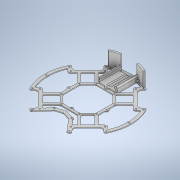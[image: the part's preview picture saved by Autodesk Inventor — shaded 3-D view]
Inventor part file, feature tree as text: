
AUTODESK INVENTOR PART (.ipt)
format: ipt  version: 2020 (Build 240168000, 168)  size: 1,558,528 bytes
history: native  units: mm
features: projected_geometry x25, extrude x17, sketch x11, other x4, fillet x3, chamfer x1
ambient origin geometry x8: Origin, YZ Plane, XZ Plane, XY Plane, X Axis, Y Axis, Z Axis, Center Point
bodies: Body1 (feature_tree)
feature tree (61):
  other  "Твердое тело1"
  extrude  "outer"  TaperAngle=45.0deg  [1 undecoded]
  extrude  "inner"  Depth=7.0mm
  sketch  "Эскиз3"
  extrude  "Выдавливание3"  Depth=20.0mm
  extrude  "Выдавливание4"  Depth=7.0mm
  sketch  "Эскиз4"
  extrude  "Выдавливание5"  Depth=3.2mm
  extrude  "Выдавливание6"  Depth=59.0mm
  sketch  "Эскиз5"
  extrude  "Выдавливание7"  Depth=83.0mm
  extrude  "Выдавливание8"  Depth=69.0mm
  sketch  "Эскиз6"
  extrude  "Выдавливание9"  Depth=55.0mm
  extrude  "Выдавливание10"  Depth=3.0mm
  other  "РабПлоскость1"
  extrude  "Выдавливание11"  Depth=8.0mm
  chamfer  "Фаска1"  Distance=5.0mm
  fillet  "Сопряжение1"  Radius=2.0mm
  fillet  "Сопряжение2"  Radius=40.0mm
  other  "РабПлоскость2"
  extrude  "Выдавливание12"  Depth=2.0mm
  sketch  "Эскиз9"
  extrude  "Выдавливание13"  Depth=105.0mm
  extrude  "Выдавливание14"  Depth=2.0mm
  other  "РабПлоскость3"
  extrude  "Выдавливание15"  Depth=2.0mm TaperAngle=0.0deg
  extrude  "Выдавливание16"  Depth=3.5mm
  fillet  "Сопряжение3"  Radius=2.0mm
  extrude  "Выдавливание17"  Depth=6.0mm
  sketch  "Эскиз1"
  sketch  "Эскиз2"
  projected_geometry  "Спроецированная петля1"
  projected_geometry  "Спроецированная петля2"
  projected_geometry  "Спроецированная петля3"
  projected_geometry  "Спроецированная петля4"
  projected_geometry  "Спроецированная петля5"
  sketch  "Эскиз7"
  projected_geometry  "Спроецированная петля6"
  projected_geometry  "Спроецированная петля7"
  projected_geometry  "Спроецированная петля8"
  sketch  "Эскиз8"
  projected_geometry  "Спроецированная петля9"
  projected_geometry  "Спроецированная петля10"
  projected_geometry  "Спроецированная петля11"
  projected_geometry  "Спроецированная петля12"
  projected_geometry  "Спроецированная петля13"
  projected_geometry  "Спроецированная петля14"
  projected_geometry  "Спроецированная петля15"
  sketch  "Эскиз10"
  projected_geometry  "Спроецированная петля16"
  projected_geometry  "Спроецированная петля17"
  projected_geometry  "Спроецированная петля18"
  projected_geometry  "Спроецированная петля19"
  projected_geometry  "Спроецированная петля20"
  projected_geometry  "Спроецированная петля21"
  projected_geometry  "Спроецированная петля22"
  projected_geometry  "Спроецированная петля23"
  projected_geometry  "Спроецированная петля24"
  projected_geometry  "Спроецированная петля25"
  sketch  "Эскиз11"
note: 1 required parameter value undecoded (feature->parameter linkage not recoverable at this tier; creation-order binding heuristic only, values carry confidence <= 0.55)
